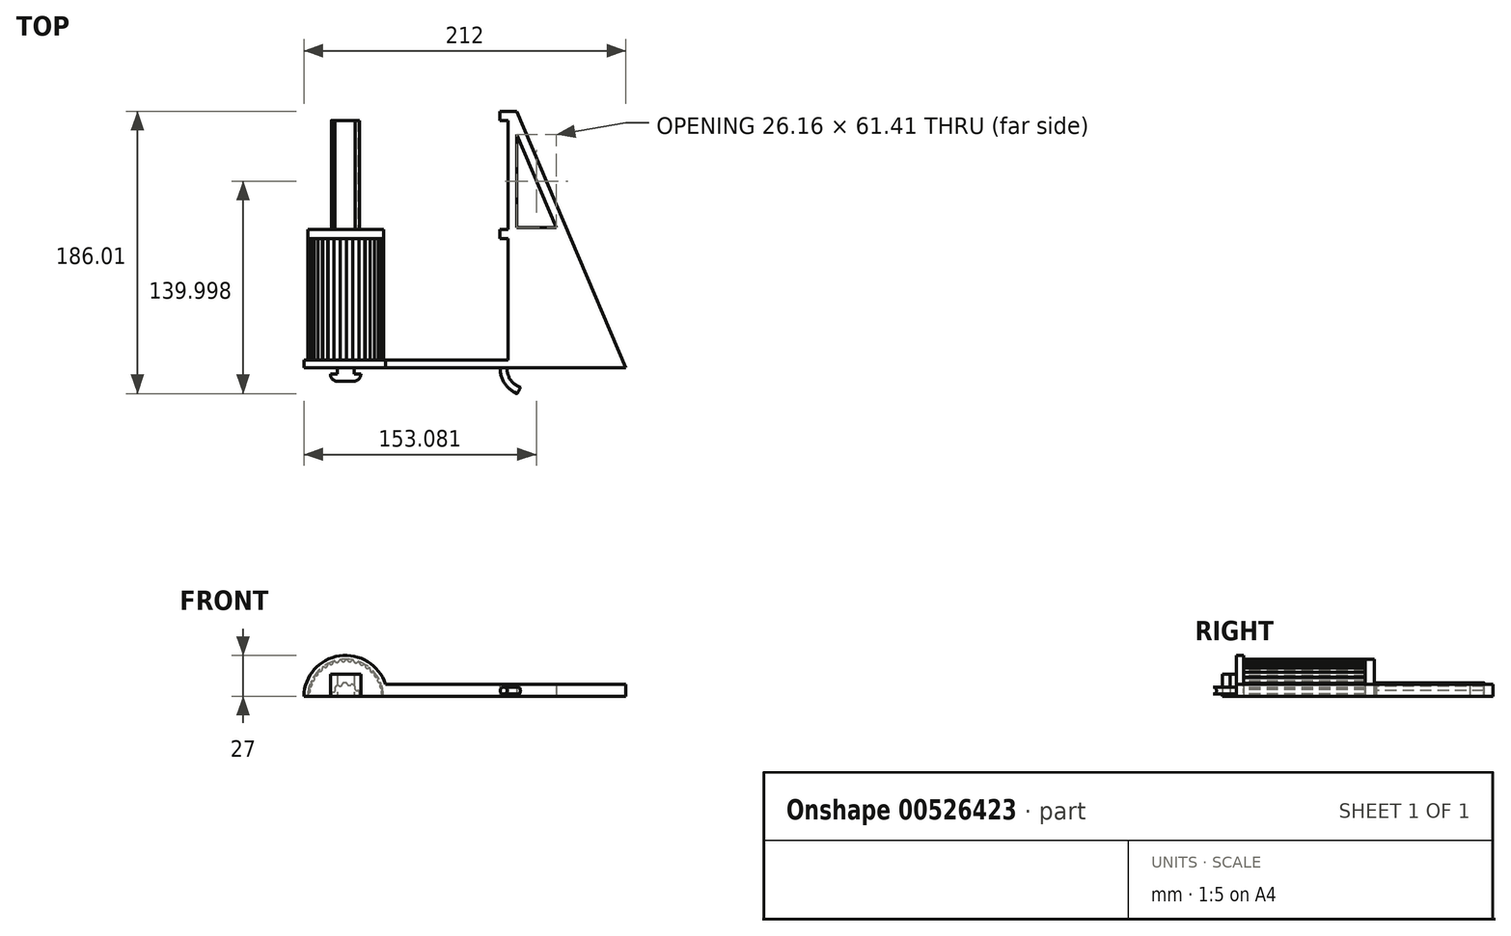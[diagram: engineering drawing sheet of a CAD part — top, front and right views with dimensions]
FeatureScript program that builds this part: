
annotation { "Feature Type Name" : "Feature", "Feature Type Description" : "" }
export const myFeature = defineFeature(function(context is Context, id is Id, definition is map)
    precondition{}
    {
        {
            var Q0;
            Q0=qCreatedBy(makeId("Front.planeOp"),FACE);
            var sketch = newSketch(context, id + "F0", { "sketchPlane" : qUnion([Q0])});
            skArc(sketch, "E0", {"start": v(26.15, 8.5) * mm, "mid": v(-4.3, 27.16) * mm, "end": v(-27.5, 0) * mm});
            skLineSegment(sketch, "E1", {"start": v(27.5, 0) * mm, "end": v(112.5, 0) * mm});
            skLineSegment(sketch, "E2", {"start": v(27.5, 0) * mm, "end": v(-27.5, 0) * mm});
            skLineSegment(sketch, "E3", {"start": v(112.5, 0) * mm, "end": v(112.5, 8.5) * mm});
            skLineSegment(sketch, "E4", {"start": v(112.5, 8.5) * mm, "end": v(26.15, 8.5) * mm});
            skSolve(sketch);
        }
        {
            var Q0;
            Q0=makeQuery(id+"F0.imprint","IMPRINT",FACE,{"disambiguationData":[TD([[makeQuery(id+"F0.imprint","IMPRINT",EDGE,{"derivedFrom":sQuery(id+"F0.wireOp",EDGE,"E0")}),1.0]])]});
            extrude(context, id + "F1", {"entities" : qUnion([Q0]), "oppositeDirection" : true, "depth" : 5 * mm, "offsetDistance" : 25 * mm});
        }
        {
            var Q0;
            Q0=qCreatedBy(makeId("Top.planeOp"),FACE);
            var sketch = newSketch(context, id + "F2", { "sketchPlane" : qUnion([Q0])});
            skLineSegment(sketch, "E5", {"start": v(112.5, 5) * mm, "end": v(112.5, 169) * mm});
            skLineSegment(sketch, "E6", {"start": v(112.5, 169) * mm, "end": v(101.5, 169) * mm});
            skLineSegment(sketch, "E7", {"start": v(101.5, 169) * mm, "end": v(101.5, 163) * mm});
            skLineSegment(sketch, "E8", {"start": v(101.5, 163) * mm, "end": v(107, 163) * mm});
            skLineSegment(sketch, "E9", {"start": v(107, 163) * mm, "end": v(107, 91) * mm});
            skLineSegment(sketch, "E10", {"start": v(107, 91) * mm, "end": v(101.5, 91) * mm});
            skLineSegment(sketch, "E11", {"start": v(101.5, 91) * mm, "end": v(101.5, 85) * mm});
            skLineSegment(sketch, "E12", {"start": v(101.5, 85) * mm, "end": v(107, 85) * mm});
            skLineSegment(sketch, "E13", {"start": v(107, 85) * mm, "end": v(107, 5) * mm});
            skLineSegment(sketch, "E14", {"start": v(112.5, 0) * mm, "end": v(184.5, 0) * mm});
            skLineSegment(sketch, "E15", {"start": v(184.5, 0) * mm, "end": v(112.5, 169) * mm});
            skLineSegment(sketch, "E16", {"start": v(112.5, 5) * mm, "end": v(175.85, 5) * mm});
            skLineSegment(sketch, "E17", {"start": v(175.85, 5) * mm, "end": v(141.22, 86.28) * mm});
            skLineSegment(sketch, "E18", {"start": v(141.22, 86.28) * mm, "end": v(112.5, 86.28) * mm});
            skLineSegment(sketch, "E19", {"start": v(112.5, 153.7) * mm, "end": v(138.66, 92.28) * mm});
            skLineSegment(sketch, "E20", {"start": v(138.66, 92.28) * mm, "end": v(112.5, 92.28) * mm});
            skLineSegment(sketch, "E21", {"start": v(112.5, 0) * mm, "end": v(112.5, 5) * mm});
            skLineSegment(sketch, "E22", {"start": v(107, 5) * mm, "end": v(112.5, 5) * mm});
            skSolve(sketch);
        }
        {
            var Q0;
            {var subQ0=sQuery(id+"F2.wireOp",EDGE,"E6");Q0=makeQuery(id+"F2.imprint","IMPRINT",FACE,{"disambiguationData":[TD([[makeQuery(id+"F2.imprint","IMPRINT",EDGE,{"derivedFrom":subQ0}),1.0]])]});}
            extrude(context, id + "F3", {"entities" : qUnion([Q0]), "operationType" : NewBodyOperationType.ADD, "depth" : 8.5 * mm, "offsetDistance" : 25 * mm});
        }
        {
            var Q0;
            Q0 = qSketchRegion(id + "F2", true);
            extrude(context, id + "F4", {"entities" : qUnion([Q0]), "operationType" : NewBodyOperationType.ADD, "depth" : 8.5 * mm, "offsetDistance" : 25 * mm});
        }
        {
            var Q0;
            Q0=qCreatedBy(makeId("Front.planeOp"),FACE);
            var sketch = newSketch(context, id + "F5", { "sketchPlane" : qUnion([Q0])});
            skLineSegment(sketch, "E23", {"start": v(-23.5, 0) * mm, "end": v(25, 0) * mm});
            skPoint(sketch, "E24.visualSharp", {"position": v(-24.96, 1.5) * mm});
            skArc(sketch, "E24.filletArc", {"start": v(-24.88, 2.1) * mm, "mid": v(-24.7, 1.65) * mm, "end": v(-24.34, 1.35) * mm});
            skPoint(sketch, "E25.visualSharp", {"position": v(-24.96, -1.5) * mm});
            skArc(sketch, "E26.1.0", {"start": v(-24.22, 2.74) * mm, "mid": v(-23.17, 3.92) * mm, "end": v(-23.77, 5.4) * mm});
            skArc(sketch, "E26.1.1", {"start": v(-24.18, 6.22) * mm, "mid": v(-24.08, 5.75) * mm, "end": v(-23.77, 5.4) * mm});
            skArc(sketch, "E26.1.2", {"start": v(-24.22, 2.74) * mm, "mid": v(-24.63, 2.5) * mm, "end": v(-24.88, 2.1) * mm});
            skArc(sketch, "E26.2.0", {"start": v(-23.42, 6.74) * mm, "mid": v(-22.19, 7.74) * mm, "end": v(-22.54, 9.28) * mm});
            skArc(sketch, "E26.2.1", {"start": v(-22.8, 10.17) * mm, "mid": v(-22.78, 9.7) * mm, "end": v(-22.54, 9.28) * mm});
            skArc(sketch, "E26.2.2", {"start": v(-23.42, 6.74) * mm, "mid": v(-23.87, 6.57) * mm, "end": v(-24.18, 6.22) * mm});
            skArc(sketch, "E26.3.0", {"start": v(-21.97, 10.56) * mm, "mid": v(-20.59, 11.34) * mm, "end": v(-20.67, 12.92) * mm});
            skArc(sketch, "E26.3.1", {"start": v(-20.79, 13.84) * mm, "mid": v(-20.84, 13.36) * mm, "end": v(-20.67, 12.92) * mm});
            skArc(sketch, "E26.3.2", {"start": v(-21.97, 10.56) * mm, "mid": v(-22.43, 10.47) * mm, "end": v(-22.8, 10.17) * mm});
            skArc(sketch, "E26.4.0", {"start": v(-19.9, 14.08) * mm, "mid": v(-18.4, 14.61) * mm, "end": v(-18.22, 16.19) * mm});
            skArc(sketch, "E26.4.1", {"start": v(-18.19, 17.11) * mm, "mid": v(-18.32, 16.66) * mm, "end": v(-18.22, 16.19) * mm});
            skArc(sketch, "E26.4.2", {"start": v(-19.9, 14.08) * mm, "mid": v(-20.37, 14.07) * mm, "end": v(-20.79, 13.84) * mm});
            skArc(sketch, "E26.5.0", {"start": v(-17.26, 17.2) * mm, "mid": v(-15.7, 17.48) * mm, "end": v(-15.26, 19) * mm});
            skArc(sketch, "E26.5.1", {"start": v(-15.07, 19.9) * mm, "mid": v(-15.28, 19.48) * mm, "end": v(-15.26, 19) * mm});
            skArc(sketch, "E26.5.2", {"start": v(-17.26, 17.2) * mm, "mid": v(-17.74, 17.27) * mm, "end": v(-18.19, 17.11) * mm});
            skArc(sketch, "E26.6.0", {"start": v(-14.15, 19.85) * mm, "mid": v(-12.56, 19.86) * mm, "end": v(-11.87, 21.29) * mm});
            skArc(sketch, "E26.6.1", {"start": v(-11.54, 22.15) * mm, "mid": v(-11.81, 21.76) * mm, "end": v(-11.87, 21.29) * mm});
            skArc(sketch, "E26.6.2", {"start": v(-14.15, 19.85) * mm, "mid": v(-14.6, 20) * mm, "end": v(-15.07, 19.9) * mm});
            skArc(sketch, "E26.7.0", {"start": v(-10.64, 21.93) * mm, "mid": v(-9.07, 21.68) * mm, "end": v(-8.15, 22.97) * mm});
            skArc(sketch, "E26.7.1", {"start": v(-7.67, 23.76) * mm, "mid": v(-8.01, 23.43) * mm, "end": v(-8.15, 22.97) * mm});
            skArc(sketch, "E26.7.2", {"start": v(-10.64, 21.93) * mm, "mid": v(-11.06, 22.15) * mm, "end": v(-11.54, 22.15) * mm});
            skArc(sketch, "E26.8.0", {"start": v(-6.82, 23.4) * mm, "mid": v(-5.32, 22.89) * mm, "end": v(-4.2, 24) * mm});
            skArc(sketch, "E26.8.1", {"start": v(-3.6, 24.71) * mm, "mid": v(-3.99, 24.43) * mm, "end": v(-4.2, 24) * mm});
            skArc(sketch, "E26.8.2", {"start": v(-6.82, 23.4) * mm, "mid": v(-7.2, 23.69) * mm, "end": v(-7.67, 23.76) * mm});
            skArc(sketch, "E26.9.0", {"start": v(-2.82, 24.21) * mm, "mid": v(-1.43, 23.46) * mm, "end": v(-0.13, 24.37) * mm});
            skArc(sketch, "E26.9.1", {"start": v(0.58, 24.96) * mm, "mid": v(0.15, 24.76) * mm, "end": v(-0.13, 24.37) * mm});
            skArc(sketch, "E26.9.2", {"start": v(-2.82, 24.21) * mm, "mid": v(-3.15, 24.56) * mm, "end": v(-3.6, 24.71) * mm});
            skArc(sketch, "E26.10.0", {"start": v(1.26, 24.34) * mm, "mid": v(2.51, 23.37) * mm, "end": v(3.94, 24.05) * mm});
            skArc(sketch, "E26.10.1", {"start": v(4.74, 24.52) * mm, "mid": v(4.28, 24.38) * mm, "end": v(3.94, 24.05) * mm});
            skArc(sketch, "E26.10.2", {"start": v(1.26, 24.34) * mm, "mid": v(1, 24.74) * mm, "end": v(0.58, 24.96) * mm});
            skArc(sketch, "E26.11.0", {"start": v(5.3, 23.79) * mm, "mid": v(6.38, 22.62) * mm, "end": v(7.9, 23.06) * mm});
            skArc(sketch, "E26.11.1", {"start": v(8.77, 23.38) * mm, "mid": v(8.3, 23.33) * mm, "end": v(7.9, 23.06) * mm});
            skArc(sketch, "E26.11.2", {"start": v(5.3, 23.79) * mm, "mid": v(5.11, 24.22) * mm, "end": v(4.74, 24.52) * mm});
            skArc(sketch, "E26.12.0", {"start": v(9.2, 22.57) * mm, "mid": v(10.07, 21.24) * mm, "end": v(11.64, 21.42) * mm});
            skArc(sketch, "E26.12.1", {"start": v(12.55, 21.59) * mm, "mid": v(12.07, 21.61) * mm, "end": v(11.64, 21.42) * mm});
            skArc(sketch, "E26.12.2", {"start": v(9.2, 22.57) * mm, "mid": v(9.09, 23.03) * mm, "end": v(8.77, 23.38) * mm});
            skArc(sketch, "E26.13.0", {"start": v(12.85, 20.71) * mm, "mid": v(13.47, 19.26) * mm, "end": v(15.05, 19.17) * mm});
            skArc(sketch, "E26.13.1", {"start": v(15.98, 19.2) * mm, "mid": v(15.51, 19.3) * mm, "end": v(15.05, 19.17) * mm});
            skArc(sketch, "E26.13.2", {"start": v(12.85, 20.71) * mm, "mid": v(12.8, 21.19) * mm, "end": v(12.55, 21.59) * mm});
            skArc(sketch, "E26.14.0", {"start": v(16.13, 18.28) * mm, "mid": v(16.5, 16.74) * mm, "end": v(18.04, 16.39) * mm});
            skArc(sketch, "E26.14.1", {"start": v(18.96, 16.25) * mm, "mid": v(18.52, 16.43) * mm, "end": v(18.04, 16.39) * mm});
            skArc(sketch, "E26.14.2", {"start": v(16.13, 18.28) * mm, "mid": v(16.16, 18.75) * mm, "end": v(15.98, 19.2) * mm});
            skArc(sketch, "E26.15.0", {"start": v(18.95, 15.33) * mm, "mid": v(19.06, 13.75) * mm, "end": v(20.53, 13.14) * mm});
            skArc(sketch, "E26.15.1", {"start": v(21.4, 12.86) * mm, "mid": v(21, 13.1) * mm, "end": v(20.53, 13.14) * mm});
            skArc(sketch, "E26.15.2", {"start": v(18.95, 15.33) * mm, "mid": v(19.07, 15.79) * mm, "end": v(18.96, 16.25) * mm});
            skArc(sketch, "E26.16.0", {"start": v(21.25, 11.95) * mm, "mid": v(21.09, 10.37) * mm, "end": v(22.43, 9.53) * mm});
            skArc(sketch, "E26.16.1", {"start": v(23.25, 9.1) * mm, "mid": v(22.9, 9.42) * mm, "end": v(22.43, 9.53) * mm});
            skArc(sketch, "E26.16.2", {"start": v(21.25, 11.95) * mm, "mid": v(21.44, 12.38) * mm, "end": v(21.4, 12.86) * mm});
            skArc(sketch, "E26.17.0", {"start": v(22.94, 8.23) * mm, "mid": v(22.52, 6.7) * mm, "end": v(23.7, 5.65) * mm});
            skArc(sketch, "E26.17.1", {"start": v(24.45, 5.1) * mm, "mid": v(24.15, 5.46) * mm, "end": v(23.7, 5.65) * mm});
            skArc(sketch, "E26.17.2", {"start": v(22.94, 8.23) * mm, "mid": v(23.2, 8.63) * mm, "end": v(23.25, 9.1) * mm});
            skArc(sketch, "E26.18.0", {"start": v(24, 4.28) * mm, "mid": v(23.33, 2.85) * mm, "end": v(24.32, 1.61) * mm});
            skArc(sketch, "E26.18.1", {"start": v(24.95, 0.94) * mm, "mid": v(24.72, 1.35) * mm, "end": v(24.32, 1.61) * mm});
            skArc(sketch, "E26.18.2", {"start": v(24, 4.28) * mm, "mid": v(24.32, 4.63) * mm, "end": v(24.45, 5.1) * mm});
            skArc(sketch, "E26.19.0", {"start": v(24.37, 0.22) * mm, "mid": v(24.19, 0.12) * mm, "end": v(24.02, 0) * mm});
            skArc(sketch, "E26.19.2", {"start": v(24.37, 0.22) * mm, "mid": v(24.75, 0.5) * mm, "end": v(24.95, 0.94) * mm});
            skPoint(sketch, "E26.center", {"position": v(0, 0) * mm});
            skPoint(sketch, "E27.center.orphan", {"position": v(-25, 0) * mm});
            skLineSegment(sketch, "E28", {"start": v(-24.34, 1.35) * mm, "end": v(-25, 0) * mm});
            skLineSegment(sketch, "E29", {"start": v(-25, 0) * mm, "end": v(-23.5, 0) * mm});
            skPoint(sketch, "E30.orphan", {"position": v(4.98, 24.5) * mm});
            skPoint(sketch, "E31.orphan", {"position": v(4.5, 24.6) * mm});
            skPoint(sketch, "E32.orphan", {"position": v(9, 23.32) * mm});
            skPoint(sketch, "E33.orphan", {"position": v(8.55, 23.5) * mm});
            skPoint(sketch, "E34.orphan", {"position": v(12.35, 21.73) * mm});
            skPoint(sketch, "E35.orphan", {"position": v(12.77, 21.5) * mm});
            skPoint(sketch, "E36.orphan", {"position": v(16.18, 19.06) * mm});
            skPoint(sketch, "E37.orphan", {"position": v(15.8, 19.37) * mm});
            skPoint(sketch, "E38.orphan", {"position": v(19.14, 16.09) * mm});
            skPoint(sketch, "E39.orphan", {"position": v(18.82, 16.45) * mm});
            skPoint(sketch, "E40.orphan", {"position": v(21.55, 12.66) * mm});
            skPoint(sketch, "E41.orphan", {"position": v(21.3, 13.08) * mm});
            skPoint(sketch, "E42.orphan", {"position": v(23.2, 9.34) * mm});
            skPoint(sketch, "E43.orphan", {"position": v(23.37, 8.89) * mm});
            skPoint(sketch, "E44.orphan", {"position": v(24.42, 5.33) * mm});
            skPoint(sketch, "E45.orphan", {"position": v(24.52, 4.86) * mm});
            skPoint(sketch, "E46.orphan", {"position": v(24.97, 1.18) * mm});
            skPoint(sketch, "E47.orphan", {"position": v(25, 0.7) * mm});
            skPoint(sketch, "E48.orphan", {"position": v(0.82, 24.99) * mm});
            skPoint(sketch, "E49.orphan", {"position": v(0.34, 25) * mm});
            skPoint(sketch, "E50.orphan", {"position": v(-3.84, 24.7) * mm});
            skPoint(sketch, "E51.orphan", {"position": v(-7.91, 23.71) * mm});
            skPoint(sketch, "E52.orphan", {"position": v(-11.76, 22.06) * mm});
            skPoint(sketch, "E53.orphan", {"position": v(-15.28, 19.79) * mm});
            skPoint(sketch, "E54.orphan", {"position": v(-18.37, 16.96) * mm});
            skPoint(sketch, "E55.orphan", {"position": v(-20.94, 13.65) * mm});
            skPoint(sketch, "E56.orphan", {"position": v(-22.73, 10.4) * mm});
            skPoint(sketch, "E57.orphan", {"position": v(-22.93, 9.96) * mm});
            skPoint(sketch, "E58.orphan", {"position": v(-24.15, 6.46) * mm});
            skPoint(sketch, "E59.orphan", {"position": v(-24.27, 6) * mm});
            skPoint(sketch, "E60.orphan", {"position": v(-24.9, 2.34) * mm});
            skPoint(sketch, "E61.orphan", {"position": v(-24.93, 1.85) * mm});
            skSolve(sketch);
        }
        {
            var Q0;
            Q0 = qSketchRegion(id + "F5", true);
            extrude(context, id + "F6", {"entities" : qUnion([Q0]), "operationType" : NewBodyOperationType.ADD, "oppositeDirection" : true, "depth" : 85 * mm, "offsetDistance" : 25 * mm});
        }
        {
            var Q0;
            Q0=makeQuery(id+"F6.opExtrude","CAP_FACE",FACE,{"disambiguationData":[OSD([sQuery(id+"F5.wireOp",EDGE,"E23"),sQuery(id+"F5.wireOp",EDGE,"E24.filletArc"),sQuery(id+"F5.wireOp",EDGE,"E26.1.0"),sQuery(id+"F5.wireOp",EDGE,"E26.1.1"),sQuery(id+"F5.wireOp",EDGE,"E26.1.2"),sQuery(id+"F5.wireOp",EDGE,"E26.2.0"),sQuery(id+"F5.wireOp",EDGE,"E26.2.1"),sQuery(id+"F5.wireOp",EDGE,"E26.2.2"),sQuery(id+"F5.wireOp",EDGE,"E26.3.0"),sQuery(id+"F5.wireOp",EDGE,"E26.3.1"),sQuery(id+"F5.wireOp",EDGE,"E26.3.2"),sQuery(id+"F5.wireOp",EDGE,"E26.4.0"),sQuery(id+"F5.wireOp",EDGE,"E26.4.1"),sQuery(id+"F5.wireOp",EDGE,"E26.4.2"),sQuery(id+"F5.wireOp",EDGE,"E26.5.0"),sQuery(id+"F5.wireOp",EDGE,"E26.5.1"),sQuery(id+"F5.wireOp",EDGE,"E26.5.2"),sQuery(id+"F5.wireOp",EDGE,"E26.6.0"),sQuery(id+"F5.wireOp",EDGE,"E26.6.1"),sQuery(id+"F5.wireOp",EDGE,"E26.6.2"),sQuery(id+"F5.wireOp",EDGE,"E26.7.0"),sQuery(id+"F5.wireOp",EDGE,"E26.7.1"),sQuery(id+"F5.wireOp",EDGE,"E26.7.2"),sQuery(id+"F5.wireOp",EDGE,"E26.8.0"),sQuery(id+"F5.wireOp",EDGE,"E26.8.1"),sQuery(id+"F5.wireOp",EDGE,"E26.8.2"),sQuery(id+"F5.wireOp",EDGE,"E26.9.0"),sQuery(id+"F5.wireOp",EDGE,"E26.9.1"),sQuery(id+"F5.wireOp",EDGE,"E26.9.2"),sQuery(id+"F5.wireOp",EDGE,"E26.10.0"),sQuery(id+"F5.wireOp",EDGE,"E26.10.1"),sQuery(id+"F5.wireOp",EDGE,"E26.10.2"),sQuery(id+"F5.wireOp",EDGE,"E26.11.0"),sQuery(id+"F5.wireOp",EDGE,"E26.11.1"),sQuery(id+"F5.wireOp",EDGE,"E26.11.2"),sQuery(id+"F5.wireOp",EDGE,"E26.12.0"),sQuery(id+"F5.wireOp",EDGE,"E26.12.1"),sQuery(id+"F5.wireOp",EDGE,"E26.12.2"),sQuery(id+"F5.wireOp",EDGE,"E26.13.0"),sQuery(id+"F5.wireOp",EDGE,"E26.13.1"),sQuery(id+"F5.wireOp",EDGE,"E26.13.2"),sQuery(id+"F5.wireOp",EDGE,"E26.14.0"),sQuery(id+"F5.wireOp",EDGE,"E26.14.1"),sQuery(id+"F5.wireOp",EDGE,"E26.14.2"),sQuery(id+"F5.wireOp",EDGE,"E26.15.0"),sQuery(id+"F5.wireOp",EDGE,"E26.15.1"),sQuery(id+"F5.wireOp",EDGE,"E26.15.2"),sQuery(id+"F5.wireOp",EDGE,"E26.16.0"),sQuery(id+"F5.wireOp",EDGE,"E26.16.1"),sQuery(id+"F5.wireOp",EDGE,"E26.16.2"),sQuery(id+"F5.wireOp",EDGE,"E26.17.0"),sQuery(id+"F5.wireOp",EDGE,"E26.17.1"),sQuery(id+"F5.wireOp",EDGE,"E26.17.2"),sQuery(id+"F5.wireOp",EDGE,"E26.18.0"),sQuery(id+"F5.wireOp",EDGE,"E26.18.1"),sQuery(id+"F5.wireOp",EDGE,"E26.18.2"),sQuery(id+"F5.wireOp",EDGE,"E26.19.0"),sQuery(id+"F5.wireOp",EDGE,"E26.19.2"),sQuery(id+"F5.wireOp",EDGE,"E28"),sQuery(id+"F5.wireOp",EDGE,"E29")])],"isStart":false});
            var sketch = newSketch(context, id + "F7", { "sketchPlane" : qUnion([Q0])});
            skArc(sketch, "E62", {"start": v(25, 0) * mm, "mid": v(0.1, 25) * mm, "end": v(-25, 0.22) * mm});
            skLineSegment(sketch, "E63", {"start": v(-25, 0.22) * mm, "end": v(25, 0) * mm});
            skSolve(sketch);
        }
        {
            var Q0;
            Q0 = qSketchRegion(id + "F7", true);
            extrude(context, id + "F8", {"entities" : qUnion([Q0]), "operationType" : NewBodyOperationType.ADD, "depth" : 6 * mm, "offsetDistance" : 25 * mm});
        }
        {
            var Q0;
            Q0=makeQuery(id+"F8.opExtrude","CAP_FACE",FACE,{"disambiguationData":[OSD([sQuery(id+"F7.wireOp",EDGE,"E62"),sQuery(id+"F7.wireOp",EDGE,"E63")])],"isStart":false});
            var sketch = newSketch(context, id + "F9", { "sketchPlane" : qUnion([Q0])});
            skArc(sketch, "E64", {"start": v(9.43, 1.12) * mm, "mid": v(9.33, 1.8) * mm, "end": v(9.17, 2.47) * mm});
            skArc(sketch, "E65", {"start": v(-8, 0.14) * mm, "mid": v(-8.23, 0.8) * mm, "end": v(-8.73, 1.29) * mm});
            skPoint(sketch, "E66.visualSharp", {"position": v(-9.38, 1.5) * mm});
            skArc(sketch, "E66.filletArc", {"start": v(-9.2, 2.4) * mm, "mid": v(-9.15, 1.77) * mm, "end": v(-8.73, 1.29) * mm});
            skPoint(sketch, "E67.visualSharp", {"position": v(-9.38, -1.5) * mm});
            skArc(sketch, "E68.1.0", {"start": v(-7.7, 4.3) * mm, "mid": v(-6.34, 4.88) * mm, "end": v(-6.14, 6.35) * mm});
            skArc(sketch, "E68.1.1", {"start": v(-5.82, 7.5) * mm, "mid": v(-6.17, 6.98) * mm, "end": v(-6.14, 6.35) * mm});
            skArc(sketch, "E68.1.2", {"start": v(-7.7, 4.3) * mm, "mid": v(-8.33, 4.18) * mm, "end": v(-8.75, 3.7) * mm});
            skArc(sketch, "E68.2.0", {"start": v(-3.49, 8.11) * mm, "mid": v(-2.05, 7.73) * mm, "end": v(-1, 8.77) * mm});
            skArc(sketch, "E68.2.1", {"start": v(-0.03, 9.5) * mm, "mid": v(-0.63, 9.3) * mm, "end": v(-1, 8.77) * mm});
            skArc(sketch, "E68.2.2", {"start": v(-3.49, 8.11) * mm, "mid": v(-4.06, 8.39) * mm, "end": v(-4.68, 8.27) * mm});
            skArc(sketch, "E68.3.0", {"start": v(2.18, 8.55) * mm, "mid": v(3.09, 7.38) * mm, "end": v(4.56, 7.56) * mm});
            skArc(sketch, "E68.3.1", {"start": v(5.77, 7.55) * mm, "mid": v(5.17, 7.76) * mm, "end": v(4.56, 7.56) * mm});
            skArc(sketch, "E68.3.2", {"start": v(2.18, 8.55) * mm, "mid": v(1.9, 9.12) * mm, "end": v(1.33, 9.4) * mm});
            skArc(sketch, "E68.4.0", {"start": v(6.95, 5.45) * mm, "mid": v(6.95, 3.96) * mm, "end": v(8.23, 3.2) * mm});
            skArc(sketch, "E68.4.1", {"start": v(9.17, 2.47) * mm, "mid": v(8.82, 3) * mm, "end": v(8.23, 3.2) * mm});
            skArc(sketch, "E68.4.2", {"start": v(6.95, 5.45) * mm, "mid": v(7.07, 6.07) * mm, "end": v(6.8, 6.64) * mm});
            skArc(sketch, "E68.5.2", {"start": v(8.83, 0.08) * mm, "mid": v(9.3, 0.5) * mm, "end": v(9.43, 1.12) * mm});
            skLineSegment(sketch, "E69", {"start": v(-8, 0.14) * mm, "end": v(8.83, 0.08) * mm});
            skArc(sketch, "E70.trimOffspring", {"start": v(-8.75, 3.7) * mm, "mid": v(-9, 3.06) * mm, "end": v(-9.2, 2.4) * mm});
            skArc(sketch, "E71.trimOffspring", {"start": v(-4.68, 8.27) * mm, "mid": v(-5.26, 7.9) * mm, "end": v(-5.82, 7.5) * mm});
            skArc(sketch, "E72.trimOffspring", {"start": v(1.33, 9.4) * mm, "mid": v(0.65, 9.48) * mm, "end": v(-0.03, 9.5) * mm});
            skArc(sketch, "E73.trimOffspring", {"start": v(6.8, 6.64) * mm, "mid": v(6.3, 7.11) * mm, "end": v(5.77, 7.55) * mm});
            skSolve(sketch);
        }
        {
            var Q0;
            Q0 = qSketchRegion(id + "F9", true);
            extrude(context, id + "F10", {"entities" : qUnion([Q0]), "operationType" : NewBodyOperationType.ADD, "depth" : 72 * mm, "offsetDistance" : 25 * mm});
        }
        {
            var Q0;
            Q0=makeQuery(id+"F4.boolean.opBoolean","MERGE",FACE,{"derivedFrom":[makeQuery(id+"F1.opExtrude","CAP_FACE",FACE,{"disambiguationData":[OSD([sQuery(id+"F0.wireOp",EDGE,"E0"),sQuery(id+"F0.wireOp",EDGE,"E1"),sQuery(id+"F0.wireOp",EDGE,"E2"),sQuery(id+"F0.wireOp",EDGE,"E3"),sQuery(id+"F0.wireOp",EDGE,"E4")])],"isStart":true}),makeQuery(id+"F4.opExtrude","SWEPT_FACE",FACE,{"disambiguationData":[OSD([sQuery(id+"F2.wireOp",EDGE,"E14")])]})]});
            var sketch = newSketch(context, id + "F11", { "sketchPlane" : qUnion([Q0])});
            skLineSegment(sketch, "E74.bottom", {"start": v(-27.5, 0) * mm, "end": v(222.5, 0) * mm});
            skLineSegment(sketch, "E74.top", {"start": v(-27.5, 0.5) * mm, "end": v(222.5, 0.5) * mm});
            skLineSegment(sketch, "E74.left", {"start": v(-27.5, 0) * mm, "end": v(-27.5, 0.5) * mm});
            skLineSegment(sketch, "E74.right", {"start": v(222.5, 0) * mm, "end": v(222.5, 0.5) * mm});
            skSolve(sketch);
        }
        {
            var Q0;
            Q0 = qSketchRegion(id + "F11", true);
            extrude(context, id + "F12", {"entities" : qUnion([Q0]), "operationType" : NewBodyOperationType.REMOVE, "endBound" : BoundingType.THROUGH_ALL, "oppositeDirection" : true, "depth" : 200 * mm, "offsetDistance" : 25 * mm});
        }
        {
            var Q0;
            Q0=qCreatedBy(makeId("Top.planeOp"),FACE);
            var sketch = newSketch(context, id + "F13", { "sketchPlane" : qUnion([Q0])});
            skLineSegment(sketch, "E75", {"start": v(0, 0) * mm, "end": v(0, -17.8) * mm, "construction": true});
            skLineSegment(sketch, "E76", {"start": v(0, 0) * mm, "end": v(-5.5, 0) * mm});
            skLineSegment(sketch, "E77", {"start": v(-5.5, 0) * mm, "end": v(-5.5, -4) * mm});
            skLineSegment(sketch, "E78", {"start": v(-5.5, -4) * mm, "end": v(-10, -4) * mm});
            skLineSegment(sketch, "E79", {"start": v(-10, -4) * mm, "end": v(-10, -4) * mm});
            skLineSegment(sketch, "E80", {"start": v(-5, -9) * mm, "end": v(0, -9) * mm});
            skPoint(sketch, "E81.visualSharp", {"position": v(-10, -9) * mm});
            skArc(sketch, "E81.filletArc", {"start": v(-10, -4) * mm, "mid": v(-8.54, -7.54) * mm, "end": v(-5, -9) * mm});
            skLineSegment(sketch, "E82.MirrorCS", {"start": v(5.5, 0) * mm, "end": v(5.5, -4) * mm});
            skLineSegment(sketch, "E83.MirrorCS", {"start": v(0, 0) * mm, "end": v(5.5, 0) * mm});
            skLineSegment(sketch, "E84.MirrorCS", {"start": v(5.5, -4) * mm, "end": v(10, -4) * mm});
            skArc(sketch, "E85.MirrorCS", {"start": v(10, -4) * mm, "mid": v(8.54, -7.54) * mm, "end": v(5, -9) * mm});
            skLineSegment(sketch, "E86.MirrorCS", {"start": v(5, -9) * mm, "end": v(0, -9) * mm});
            skSolve(sketch);
        }
        {
            var Q0;
            Q0=makeQuery(id+"F13.imprint","IMPRINT",FACE,{"disambiguationData":[TD([[makeQuery(id+"F13.imprint","IMPRINT",EDGE,{"derivedFrom":sQuery(id+"F13.wireOp",EDGE,"E76")}),1.0]])]});
            extrude(context, id + "F14", {"entities" : qUnion([Q0]), "operationType" : NewBodyOperationType.ADD, "depth" : 15 * mm, "offsetDistance" : 25 * mm, "hasSecondDirection" : true, "secondDirectionOppositeDirection" : false, "secondDirectionDepth" : 0.5 * mm});
        }
        {
            var Q0;
            {var subQ0=sQuery(id+"F2.wireOp",EDGE,"E22");var subQ1=sQuery(id+"F2.wireOp",EDGE,"E13");var subQ2=sQuery(id+"F2.wireOp",EDGE,"E12");var subQ3=sQuery(id+"F2.wireOp",EDGE,"E11");var subQ4=sQuery(id+"F2.wireOp",EDGE,"E10");var subQ5=sQuery(id+"F2.wireOp",EDGE,"E9");var subQ6=sQuery(id+"F2.wireOp",EDGE,"E8");var subQ7=sQuery(id+"F2.wireOp",EDGE,"E7");var subQ8=sQuery(id+"F2.wireOp",EDGE,"E6");var subQ9=sQuery(id+"F2.wireOp",EDGE,"E5");Q0=makeQuery(id+"F4.boolean.opBoolean","MERGE",FACE,{"derivedFrom":[makeQuery(id+"F3.boolean.opBoolean","MERGE",FACE,{"derivedFrom":[makeQuery(id+"F1.opExtrude","SWEPT_FACE",FACE,{"disambiguationData":[OSD([sQuery(id+"F0.wireOp",EDGE,"E4")])]}),makeQuery(id+"F3.opExtrude","CAP_FACE",FACE,{"disambiguationData":[OSD([subQ9,subQ8,subQ7,subQ6,subQ5,subQ4,subQ3,subQ2,subQ1,subQ0])],"isStart":false})]}),makeQuery(id+"F4.opExtrude","CAP_FACE",FACE,{"disambiguationData":[OSD([subQ9,subQ8,subQ7,subQ6,subQ5,subQ4,subQ3,subQ2,subQ1,sQuery(id+"F2.wireOp",EDGE,"E14"),sQuery(id+"F2.wireOp",EDGE,"E15"),sQuery(id+"F2.wireOp",EDGE,"E19"),sQuery(id+"F2.wireOp",EDGE,"E20"),sQuery(id+"F2.wireOp",EDGE,"E21"),subQ0])],"isStart":false})]});}
            cPlane(context, id + "F15", {"entities" : qUnion([Q0]), "cplaneType" : CPlaneType.OFFSET, "offset" : 4.25 * mm, "oppositeDirection" : true, "width" : 150 * mm, "height" : 150 * mm});
        }
        {
            var Q0;
            Q0=qCreatedBy(id+"F15.planeOp",FACE);
            var sketch = newSketch(context, id + "F16", { "sketchPlane" : qUnion([Q0])});
            skLineSegment(sketch, "E87", {"start": v(104, 0) * mm, "end": v(104, -0.73) * mm});
            skLineSegment(sketch, "E88", {"start": v(112.3, -14.15) * mm, "end": v(114, -15) * mm});
            skArc(sketch, "E89.filletArc", {"start": v(104, -0.73) * mm, "mid": v(106.24, -8.62) * mm, "end": v(112.3, -14.15) * mm});
            skSolve(sketch);
        }
        {
            var Q0;
            Q0=makeQuery(id+"F4.boolean.opBoolean","MERGE",FACE,{"derivedFrom":[makeQuery(id+"F1.opExtrude","CAP_FACE",FACE,{"disambiguationData":[OSD([sQuery(id+"F0.wireOp",EDGE,"E0"),sQuery(id+"F0.wireOp",EDGE,"E1"),sQuery(id+"F0.wireOp",EDGE,"E2"),sQuery(id+"F0.wireOp",EDGE,"E3"),sQuery(id+"F0.wireOp",EDGE,"E4")])],"isStart":true}),makeQuery(id+"F4.opExtrude","SWEPT_FACE",FACE,{"disambiguationData":[OSD([sQuery(id+"F2.wireOp",EDGE,"E14")])]})]});
            var sketch = newSketch(context, id + "F17", { "sketchPlane" : qUnion([Q0])});
            skCircle(sketch, "E90", {"center": v(104, 4.25) * mm, "radius": 2.25 * mm});
            skSolve(sketch);
        }
        {
            var Q0;
            Q0 = qSketchRegion(id + "F17", true);
            var Q1;
            Q1 = qConstructionFilter(qBodyType(qCreatedBy(id + "F16" ,EDGE), BodyType.WIRE), ConstructionObject.NO);
            sweep(context, id + "F18", {"operationType" : NewBodyOperationType.ADD, "profiles" : qUnion([Q0]), "path" : qUnion([Q1])});
        }
    });
